# Revit family: GMV-ND（18-36）PLSC1-T
name_source: partatom
category: 机械设备
revit_build: Autodesk Revit 2014 (Build: 20130308_1515(x64)
units: mm (PartAtom-declared; Revit-internal decimal feet)

## types (6) — shared parameters
Depth = 462  [stored 1.51575 ft]
Hight = 200  [stored 0.656168 ft]
Width = 710
回风口宽度 = 710
回风口高度 = 200  [stored 0.656168 ft]
室内机材质 = 热镀锌板
宽 = 710
排水管管径 = 25  [stored 0.082021 ft]
液管管径 = 6.35  [stored 0.0208333 ft]
深 = 462  [stored 1.51575 ft]
电源 = 220V~50Hz
送风口宽度 = 585  [stored 1.91929 ft]
送风口高度 = 122  [stored 0.400262 ft]
高 = 200  [stored 0.656168 ft]

## per-type parameters (varying)
| type | 净重(kg) | 气管管径 |
| GMV-ND22PLS/C1-T | 18.5 | 9.52 |
| GMV-ND25PLS/C1-T | 18.5 | 9.52 |
| GMV-ND28PLS/C1-T | 18.5 | 9.52 |
| GMV-ND32PLS/C1-T | 19 | 12.7  [stored 0.0416667 ft] |
| GMV-ND36PLS/C1-T | 19 | 12.7  [stored 0.0416667 ft] |
| GMV-ND18PLS/C1-T | 18.5 | 9.52 |

note: [stored X ft] marks values corroborated as IEEE doubles in the binary element streams (Revit-internal decimal feet)
